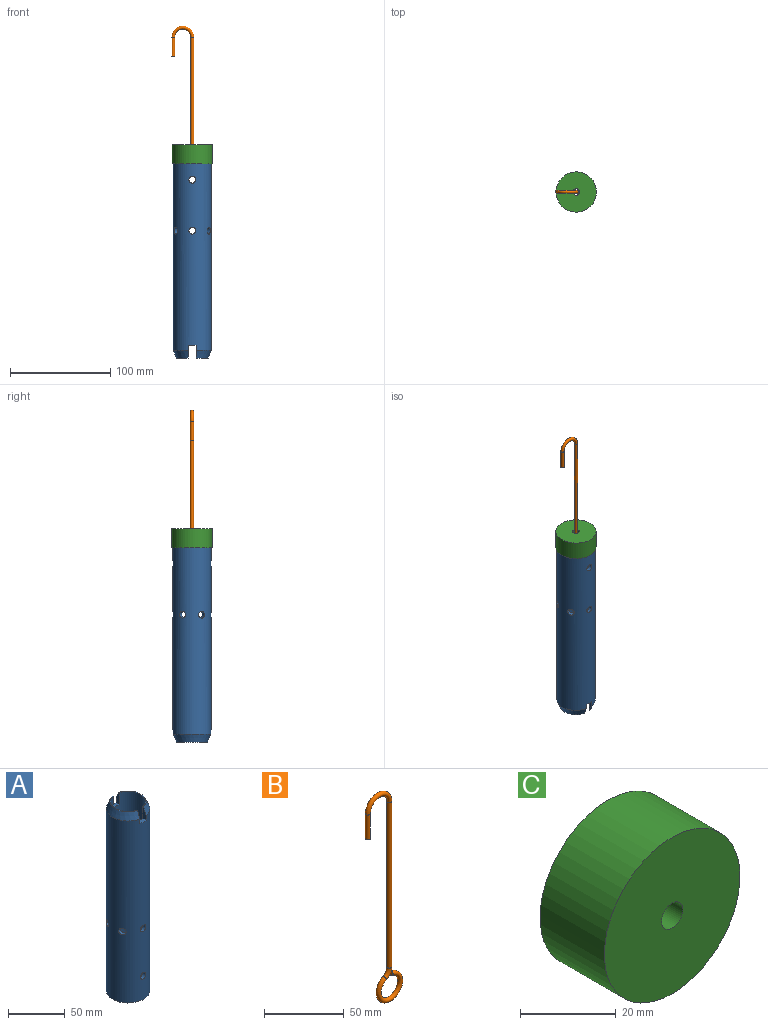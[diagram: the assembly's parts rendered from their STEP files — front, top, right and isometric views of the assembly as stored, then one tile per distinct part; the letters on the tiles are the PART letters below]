
ASSEMBLY  parts=3 mates=2
PART A: 21 faces, bbox 38.1x38.1x203.2 mm
  f0: plane 30.82x12.07mm, normal (0,0,1), area 26.1mm2, adj f6,f13,f18,f19
  f1: cylinder r=3.38mm len=7.95mm, axis (0.87,-0.5,0), area 81.7mm2, adj f6,f7
  f2: cylinder r=3.38mm len=7.95mm, axis (0.87,0.5,0), area 81.7mm2, adj f6,f7
  f3: cylinder r=3.38mm len=6.76mm, axis (0,1,0), area 81.7mm2, adj f6,f7
  f4: cylinder r=3.38mm len=7.95mm, axis (-0.87,0.5,0), area 81.7mm2, adj f6,f7
  f5: cylinder r=3.38mm len=7.95mm, axis (-0.87,-0.5,0), area 81.7mm2, adj f6,f7
  f6: cylinder r=15.24mm len=203.2mm, axis (0,0,-1), area 18973.8mm2, adj f0,f1,f2,f3,f4,f5,f8,f9
  f7: cylinder r=19.05mm len=195.58mm, axis (0,0,-1), area 23044.7mm2, adj f1,f2,f3,f4,f5,f8,f10,f11
  f8: cylinder r=3.38mm len=6.76mm, axis (0,-1,0), area 81.7mm2, adj f6,f7
  f9: plane 30.82x12.07mm, normal (0,0,1), area 26.1mm2, adj f6,f15,f17,f20
  f10: plane 38.1x38.1mm, normal (0,0,-1), area 410.4mm2, adj f6,f7
  f11: cylinder r=3.38mm len=6.76mm, axis (0,1,0), area 81.7mm2, adj f6,f7
  f12: cylinder r=3.38mm len=6.76mm, axis (0,-1,0), area 81.7mm2, adj f6,f7
  f13: plane 12.7x3.91mm, normal (-1,0,0), area 37.3mm2, adj f0,f6,f7,f14,f19
  f14: plane 7.62x4.29mm, normal (0,0,1), area 29.3mm2, adj f6,f7,f13,f15
  f15: plane 12.7x3.91mm, normal (1,0,0), area 37.3mm2, adj f6,f7,f9,f14,f20
  f16: plane 7.62x4.29mm, normal (0,0,1), area 29.3mm2, adj f6,f7,f17,f18
  f17: plane 12.7x3.91mm, normal (1,0,0), area 37.3mm2, adj f6,f7,f9,f16,f20
  f18: plane 12.7x3.91mm, normal (-1,0,0), area 37.3mm2, adj f0,f6,f7,f16,f19
  f19: cone r=15.88mm half-angle=22.6deg, axis (0,0,-1), area 389.5mm2, adj f0,f7,f13,f18
  f20: cone r=15.88mm half-angle=22.6deg, axis (0,0,-1), area 389.5mm2, adj f7,f9,f15,f17
PART B: 7 faces, bbox 33.6x3.2x166.3 mm
  f0: plane 3.18x3.13mm, normal (-0.98,0,0.17), area 7.9mm2, adj f2
  f1: plane 3.18x3.18mm, normal (0,0,-1), area 7.9mm2, adj f6
  f2: torus R=9.53mm, axis (0,1,0), area 537.3mm2, adj f0,f3
  f3: torus R=7.43mm, axis (0,-1,0), area 82.8mm2, adj f2,f4
  f4: cylinder r=1.59mm len=127mm, axis (0,0,1), area 1266.8mm2, adj f3,f5
  f5: torus R=9.53mm, axis (0,-1,0), area 298.5mm2, adj f4,f6
  f6: cylinder r=1.59mm len=19.05mm, axis (0,0,-1), area 190mm2, adj f1,f5
PART C: 4 faces, bbox 40.1x19.1x40.1 mm
  f0: cylinder r=3.17mm len=19.05mm, axis (0,1,0), area 380mm2, adj f2,f3
  f1: cylinder r=20.07mm len=40.13mm, axis (0,1,0), area 2401.8mm2, adj f2,f3
  f2: plane 40.13x40.13mm, normal (0,-1,0), area 1233.3mm2, adj f0,f1
  f3: plane 40.13x40.13mm, normal (0,1,0), area 1233.3mm2, adj f0,f1
PLACE A rot(axis=(0,1,0),180deg) t=(4.22,71.96,62.64)mm
PLACE B t=(4.22,71.93,37.24)mm
PLACE C rot(axis=(1,0,0),90deg) t=(4.22,71.96,72.16)mm
MATE pin_slot C.f1 <-> A.f6  axis (0,0,1) through (4.22,71.96,62.64)mm
MATE pin_slot A.f11 <-> B.f2  axis (0,1,0) through (4.22,52.88,37.24)mm
